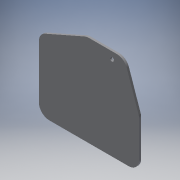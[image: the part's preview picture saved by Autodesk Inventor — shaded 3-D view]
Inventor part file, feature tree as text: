
AUTODESK INVENTOR PART (.ipt)
format: ipt  version: 2016 (Build 200138000, 138)  size: 100,352 bytes
history: native  units: mm
features: reference x9, extrude x1
ambient origin geometry x8: Origin, YZ Plane, XZ Plane, XY Plane, X Axis, Y Axis, Z Axis, Center Point
bodies: Body1 (feature_tree)
feature tree (10):
  extrude  "Extrusion3"  Depth=145.0mm
  reference  "Reference1"
  reference  "Reference5"
  reference  "Reference6"
  reference  "Reference7"
  reference  "Reference8"
  reference  "Reference9"
  reference  "Reference10"
  reference  "Reference11"
  reference  "Reference12"
